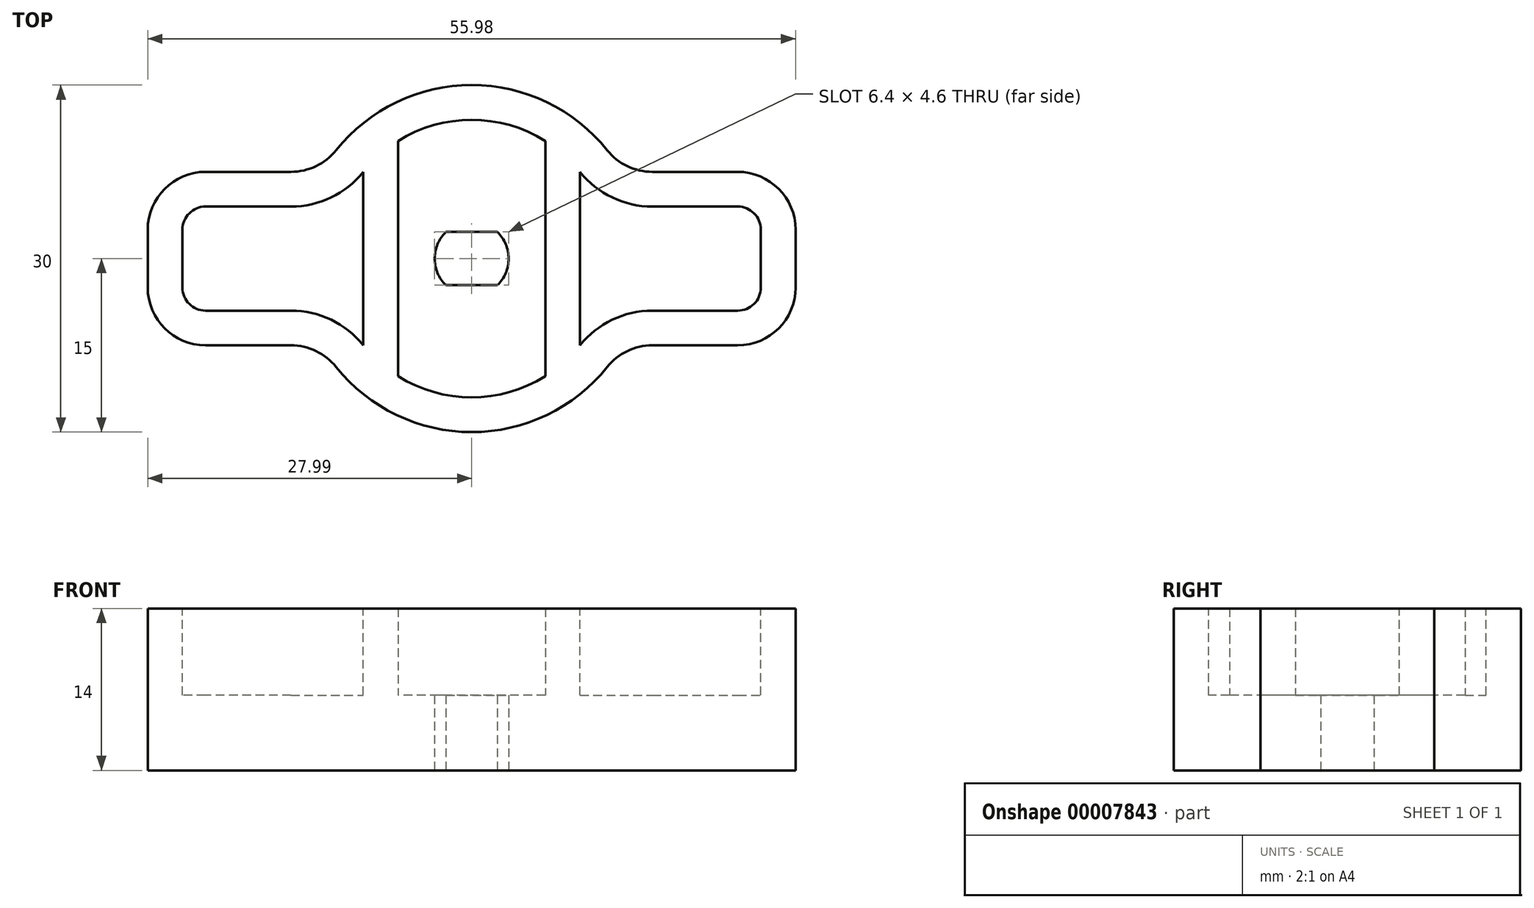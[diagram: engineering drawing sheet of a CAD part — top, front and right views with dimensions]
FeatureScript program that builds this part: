
annotation { "Feature Type Name" : "Feature", "Feature Type Description" : "" }
export const myFeature = defineFeature(function(context is Context, id is Id, definition is map)
    precondition{}
    {
        {
            var Q0;
            Q0=qCreatedBy(makeId("Top.planeOp"),FACE);
            var sketch = newSketch(context, id + "F0", { "sketchPlane" : qUnion([Q0])});
            skArc(sketch, "E0", {"start": v(-13, -7.5) * mm, "mid": v(0, -15) * mm, "end": v(13, -7.5) * mm});
            skLineSegment(sketch, "E1", {"start": v(-13, -7.5) * mm, "end": v(-28, -7.5) * mm});
            skLineSegment(sketch, "E2", {"start": v(-28, -7.5) * mm, "end": v(-28, 7.5) * mm});
            skLineSegment(sketch, "E3", {"start": v(-28, 7.5) * mm, "end": v(-13, 7.5) * mm});
            skArc(sketch, "E4", {"start": v(13, 7.5) * mm, "mid": v(0, 15) * mm, "end": v(-13, 7.5) * mm});
            skLineSegment(sketch, "E5", {"start": v(13, 7.5) * mm, "end": v(28, 7.5) * mm});
            skLineSegment(sketch, "E6", {"start": v(28, 7.5) * mm, "end": v(28, -7.5) * mm});
            skLineSegment(sketch, "E7", {"start": v(28, -7.5) * mm, "end": v(13, -7.5) * mm});
            skSolve(sketch);
        }
        {
            var Q0;
            Q0 = qSketchRegion(id + "F0", true);
            extrude(context, id + "F1", {"entities" : qUnion([Q0]), "depth" : 14 * mm, "offsetDistance" : 25 * mm});
        }
        {
            var Q0;
            Q0=qCreatedBy(makeId("Top.planeOp"),FACE);
            var sketch = newSketch(context, id + "F2", { "sketchPlane" : qUnion([Q0])});
            skArc(sketch, "E8", {"start": v(2.22, -2.3) * mm, "mid": v(3.2, 0) * mm, "end": v(2.22, 2.3) * mm});
            skLineSegment(sketch, "E9", {"start": v(-2.22, 2.3) * mm, "end": v(2.22, 2.3) * mm});
            skLineSegment(sketch, "E10", {"start": v(-2.22, -2.3) * mm, "end": v(2.22, -2.3) * mm});
            skArc(sketch, "E11", {"start": v(-2.22, 2.3) * mm, "mid": v(-3.2, 0) * mm, "end": v(-2.22, -2.3) * mm});
            skSolve(sketch);
        }
        {
            var Q0;
            Q0=makeQuery(id+"F1.opExtrude","CAP_FACE",FACE,{"disambiguationData":[OSD([sQuery(id+"F0.wireOp",EDGE,"E0"),sQuery(id+"F0.wireOp",EDGE,"E1"),sQuery(id+"F0.wireOp",EDGE,"E2"),sQuery(id+"F0.wireOp",EDGE,"E3"),sQuery(id+"F0.wireOp",EDGE,"E4"),sQuery(id+"F0.wireOp",EDGE,"E5"),sQuery(id+"F0.wireOp",EDGE,"E6"),sQuery(id+"F0.wireOp",EDGE,"E7")])],"isStart":false});
            var sketch = newSketch(context, id + "F3", { "sketchPlane" : qUnion([Q0])});
            skArc(sketch, "E12", {"start": v(11.12, 4.5) * mm, "mid": v(0, 12) * mm, "end": v(-11.12, 4.5) * mm});
            skArc(sketch, "E13", {"start": v(-11.12, -4.5) * mm, "mid": v(0, -12) * mm, "end": v(11.12, -4.5) * mm});
            skLineSegment(sketch, "E14", {"start": v(-11.12, -4.5) * mm, "end": v(-25, -4.5) * mm});
            skLineSegment(sketch, "E15", {"start": v(-25, -4.5) * mm, "end": v(-25, 4.5) * mm});
            skLineSegment(sketch, "E16", {"start": v(-25, 4.5) * mm, "end": v(-11.12, 4.5) * mm});
            skLineSegment(sketch, "E17", {"start": v(11.12, -4.5) * mm, "end": v(25, -4.5) * mm});
            skLineSegment(sketch, "E18", {"start": v(25, -4.5) * mm, "end": v(25, 4.5) * mm});
            skLineSegment(sketch, "E19", {"start": v(25, 4.5) * mm, "end": v(11.12, 4.5) * mm});
            skSolve(sketch);
        }
        {
            var Q0;
            Q0 = qSketchRegion(id + "F2", true);
            extrude(context, id + "F4", {"entities" : qUnion([Q0]), "operationType" : NewBodyOperationType.REMOVE, "endBound" : BoundingType.UP_TO_NEXT, "depth" : 6 * mm, "offsetDistance" : 25 * mm});
        }
        {
            var Q0;
            Q0 = qSketchRegion(id + "F3", true);
            extrude(context, id + "F5", {"entities" : qUnion([Q0]), "operationType" : NewBodyOperationType.REMOVE, "oppositeDirection" : true, "depth" : 14 * mm - 6.5 * mm, "offsetDistance" : 25 * mm});
        }
        {
            var Q0;
            Q0=makeQuery(id+"F1.opExtrude","SWEPT_EDGE",EDGE,{"disambiguationData":[OSD([sQuery(id+"F0.wireOp",EDGE,"E6"),sQuery(id+"F0.wireOp",EDGE,"E7")])]});
            var Q1;
            Q1=makeQuery(id+"F1.opExtrude","SWEPT_EDGE",EDGE,{"disambiguationData":[OSD([sQuery(id+"F0.wireOp",EDGE,"E5"),sQuery(id+"F0.wireOp",EDGE,"E6")])]});
            var Q2;
            Q2=makeQuery(id+"F1.opExtrude","SWEPT_EDGE",EDGE,{"disambiguationData":[OSD([sQuery(id+"F0.wireOp",EDGE,"E1"),sQuery(id+"F0.wireOp",EDGE,"E2")])]});
            var Q3;
            Q3=makeQuery(id+"F1.opExtrude","SWEPT_EDGE",EDGE,{"disambiguationData":[OSD([sQuery(id+"F0.wireOp",EDGE,"E2"),sQuery(id+"F0.wireOp",EDGE,"E3")])]});
            fillet(context, id + "F6", {"entities" : qUnion([Q0, Q1, Q2, Q3]), "radius" : 5 * mm, "tangentPropagation" : true, "allowEdgeOverflow" : false});
        }
        {
            var Q0;
            Q0=makeQuery(id+"F1.opExtrude","SWEPT_EDGE",EDGE,{"disambiguationData":[OSD([sQuery(id+"F0.wireOp",EDGE,"E3"),sQuery(id+"F0.wireOp",EDGE,"E4")])]});
            var Q1;
            Q1=makeQuery(id+"F1.opExtrude","SWEPT_EDGE",EDGE,{"disambiguationData":[OSD([sQuery(id+"F0.wireOp",EDGE,"E4"),sQuery(id+"F0.wireOp",EDGE,"E5")])]});
            var Q2;
            Q2=makeQuery(id+"F1.opExtrude","SWEPT_EDGE",EDGE,{"disambiguationData":[OSD([sQuery(id+"F0.wireOp",EDGE,"E0"),sQuery(id+"F0.wireOp",EDGE,"E7")])]});
            var Q3;
            Q3=makeQuery(id+"F1.opExtrude","SWEPT_EDGE",EDGE,{"disambiguationData":[OSD([sQuery(id+"F0.wireOp",EDGE,"E0"),sQuery(id+"F0.wireOp",EDGE,"E1")])]});
            fillet(context, id + "F7", {"entities" : qUnion([Q0, Q1, Q2, Q3]), "radius" : 5 * mm, "tangentPropagation" : true, "allowEdgeOverflow" : false});
        }
        {
            var Q0;
            Q0=makeQuery(id+"F5.boolean.opBoolean","COPY",EDGE,{"derivedFrom":makeQuery(id+"F5.opExtrude","SWEPT_EDGE",EDGE,{"disambiguationData":[OSD([sQuery(id+"F3.wireOp",EDGE,"E15"),sQuery(id+"F3.wireOp",EDGE,"E16")])]})});
            var Q1;
            Q1=makeQuery(id+"F5.boolean.opBoolean","COPY",EDGE,{"derivedFrom":makeQuery(id+"F5.opExtrude","SWEPT_EDGE",EDGE,{"disambiguationData":[OSD([sQuery(id+"F3.wireOp",EDGE,"E14"),sQuery(id+"F3.wireOp",EDGE,"E15")])]})});
            var Q2;
            Q2=makeQuery(id+"F5.boolean.opBoolean","COPY",EDGE,{"derivedFrom":makeQuery(id+"F5.opExtrude","SWEPT_EDGE",EDGE,{"disambiguationData":[OSD([sQuery(id+"F3.wireOp",EDGE,"E18"),sQuery(id+"F3.wireOp",EDGE,"E19")])]})});
            var Q3;
            Q3=makeQuery(id+"F5.boolean.opBoolean","COPY",EDGE,{"derivedFrom":makeQuery(id+"F5.opExtrude","SWEPT_EDGE",EDGE,{"disambiguationData":[OSD([sQuery(id+"F3.wireOp",EDGE,"E17"),sQuery(id+"F3.wireOp",EDGE,"E18")])]})});
            fillet(context, id + "F8", {"entities" : qUnion([Q0, Q1, Q2, Q3]), "radius" : 2 * mm, "tangentPropagation" : true, "allowEdgeOverflow" : false});
        }
        {
            var Q0;
            Q0=makeQuery(id+"F5.boolean.opBoolean","COPY",EDGE,{"derivedFrom":makeQuery(id+"F5.opExtrude","SWEPT_EDGE",EDGE,{"disambiguationData":[OSD([sQuery(id+"F3.wireOp",EDGE,"E12"),sQuery(id+"F3.wireOp",EDGE,"E16")])]})});
            var Q1;
            Q1=makeQuery(id+"F5.boolean.opBoolean","COPY",EDGE,{"derivedFrom":makeQuery(id+"F5.opExtrude","SWEPT_EDGE",EDGE,{"disambiguationData":[OSD([sQuery(id+"F3.wireOp",EDGE,"E12"),sQuery(id+"F3.wireOp",EDGE,"E19")])]})});
            var Q2;
            Q2=makeQuery(id+"F5.boolean.opBoolean","COPY",EDGE,{"derivedFrom":makeQuery(id+"F5.opExtrude","SWEPT_EDGE",EDGE,{"disambiguationData":[OSD([sQuery(id+"F3.wireOp",EDGE,"E13"),sQuery(id+"F3.wireOp",EDGE,"E14")])]})});
            var Q3;
            Q3=makeQuery(id+"F5.boolean.opBoolean","COPY",EDGE,{"derivedFrom":makeQuery(id+"F5.opExtrude","SWEPT_EDGE",EDGE,{"disambiguationData":[OSD([sQuery(id+"F3.wireOp",EDGE,"E13"),sQuery(id+"F3.wireOp",EDGE,"E17")])]})});
            fillet(context, id + "F9", {"entities" : qUnion([Q0, Q1, Q2, Q3]), "radius" : 8 * mm, "tangentPropagation" : true, "allowEdgeOverflow" : false});
        }
        {
            var Q0;
            Q0=makeQuery(id+"F5.boolean.opBoolean","COPY",FACE,{"derivedFrom":makeQuery(id+"F5.opExtrude","CAP_FACE",FACE,{"disambiguationData":[OSD([sQuery(id+"F3.wireOp",EDGE,"E12"),sQuery(id+"F3.wireOp",EDGE,"E13"),sQuery(id+"F3.wireOp",EDGE,"E14"),sQuery(id+"F3.wireOp",EDGE,"E15"),sQuery(id+"F3.wireOp",EDGE,"E16"),sQuery(id+"F3.wireOp",EDGE,"E17"),sQuery(id+"F3.wireOp",EDGE,"E18"),sQuery(id+"F3.wireOp",EDGE,"E19")])],"isStart":false})});
            var sketch = newSketch(context, id + "F10", { "sketchPlane" : qUnion([Q0])});
            skLineSegment(sketch, "E20", {"start": v(-9.37, 7.5) * mm, "end": v(-9.37, -7.5) * mm});
            skLineSegment(sketch, "E21", {"start": v(9.37, 7.5) * mm, "end": v(9.37, -7.5) * mm});
            skLineSegment(sketch, "E22", {"start": v(6.37, 10.17) * mm, "end": v(6.37, -10.17) * mm});
            skLineSegment(sketch, "E23", {"start": v(-6.37, 10.17) * mm, "end": v(-6.37, -10.17) * mm});
            skSolve(sketch);
        }
        {
            var Q0;
            {var subQ0=sQuery(id+"F10.wireOp",EDGE,"E20");Q0=makeQuery(id+"F10.imprint","IMPRINT",FACE,{"disambiguationData":[TD([[makeQuery(id+"F10.imprint","IMPRINT",EDGE,{"derivedFrom":subQ0}),1.0]])]});}
            var Q1;
            {var subQ0=sQuery(id+"F10.wireOp",EDGE,"E21");Q1=makeQuery(id+"F10.imprint","IMPRINT",FACE,{"disambiguationData":[TD([[makeQuery(id+"F10.imprint","IMPRINT",EDGE,{"derivedFrom":subQ0}),-1.0]])]});}
            var Q2;
            Q2=makeQuery(id+"F1.opExtrude","CAP_FACE",FACE,{"disambiguationData":[OSD([sQuery(id+"F0.wireOp",EDGE,"E0"),sQuery(id+"F0.wireOp",EDGE,"E1"),sQuery(id+"F0.wireOp",EDGE,"E2"),sQuery(id+"F0.wireOp",EDGE,"E3"),sQuery(id+"F0.wireOp",EDGE,"E4"),sQuery(id+"F0.wireOp",EDGE,"E5"),sQuery(id+"F0.wireOp",EDGE,"E6"),sQuery(id+"F0.wireOp",EDGE,"E7")])],"isStart":false});
            extrude(context, id + "F11", {"entities" : qUnion([Q0, Q1]), "operationType" : NewBodyOperationType.ADD, "endBound" : BoundingType.UP_TO_SURFACE, "depth" : 25 * mm, "endBoundEntityFace" : qUnion([Q2]), "offsetDistance" : 25 * mm});
        }
    });
